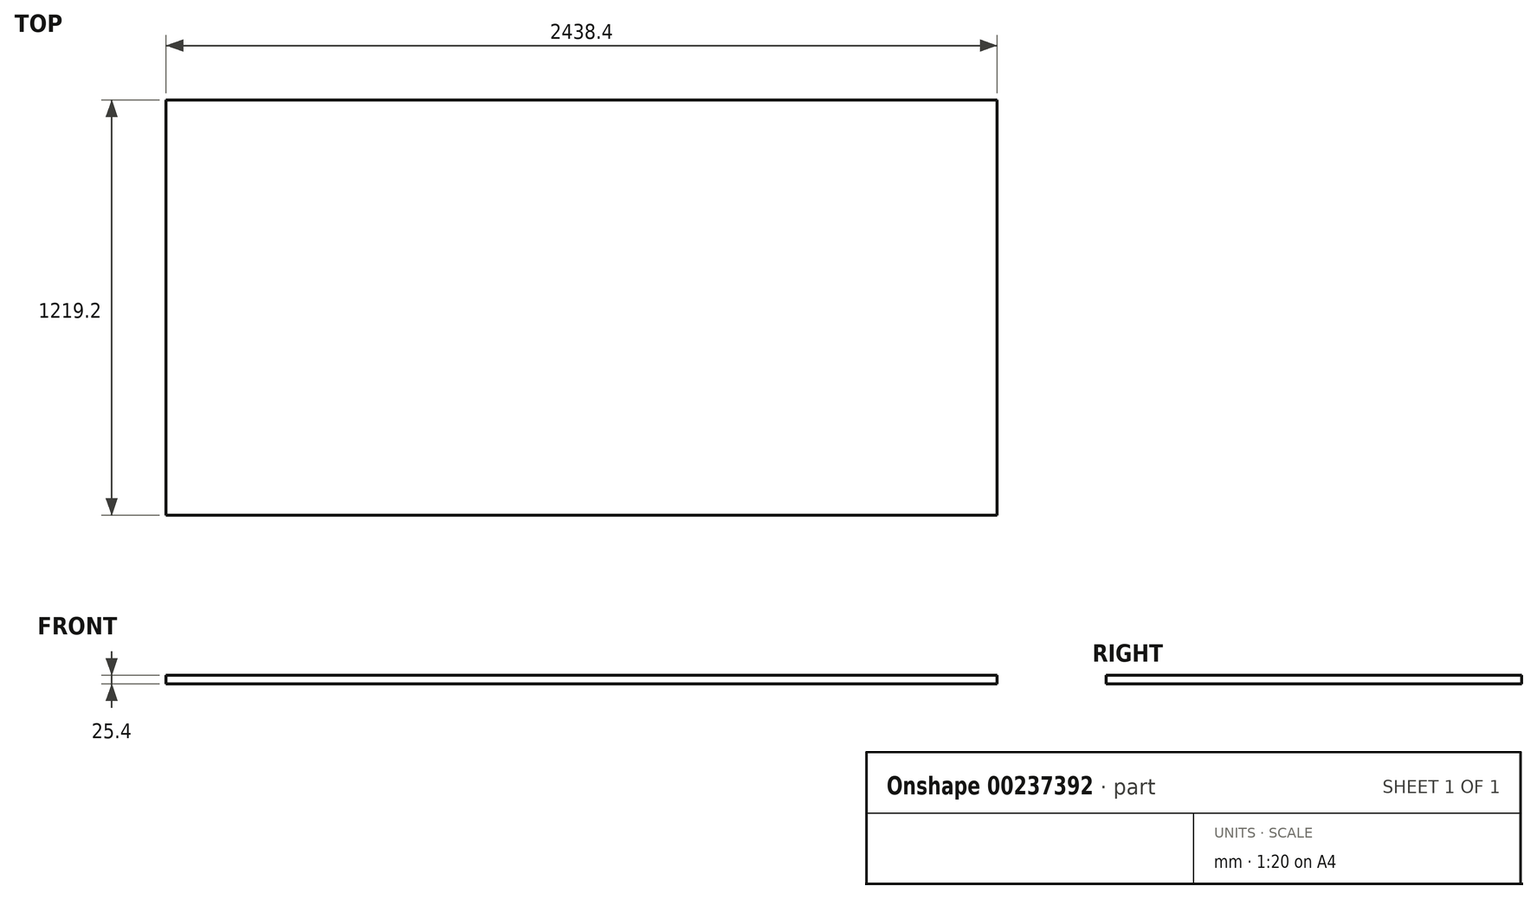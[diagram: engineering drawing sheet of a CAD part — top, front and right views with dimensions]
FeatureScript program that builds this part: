
annotation { "Feature Type Name" : "Feature", "Feature Type Description" : "" }
export const myFeature = defineFeature(function(context is Context, id is Id, definition is map)
    precondition{}
    {
        {
            var Q0;
            Q0=qCreatedBy(makeId("Top.planeOp"),FACE);
            var sketch = newSketch(context, id + "F0", { "sketchPlane" : qUnion([Q0])});
            skLineSegment(sketch, "E0.bottom", {"start": v(0, 0) * mm, "end": v(2438.4, 0) * mm});
            skLineSegment(sketch, "E0.top", {"start": v(0, 1219.2) * mm, "end": v(2438.4, 1219.2) * mm});
            skLineSegment(sketch, "E0.left", {"start": v(0, 0) * mm, "end": v(0, 1219.2) * mm});
            skLineSegment(sketch, "E0.right", {"start": v(2438.4, 0) * mm, "end": v(2438.4, 1219.2) * mm});
            skSolve(sketch);
        }
        {
            var Q0;
            Q0 = qSketchRegion(id + "F0", true);
            extrude(context, id + "F1", {"entities" : qUnion([Q0]), "oppositeDirection" : true, "depth" : 25.4 * mm});
        }
    });
